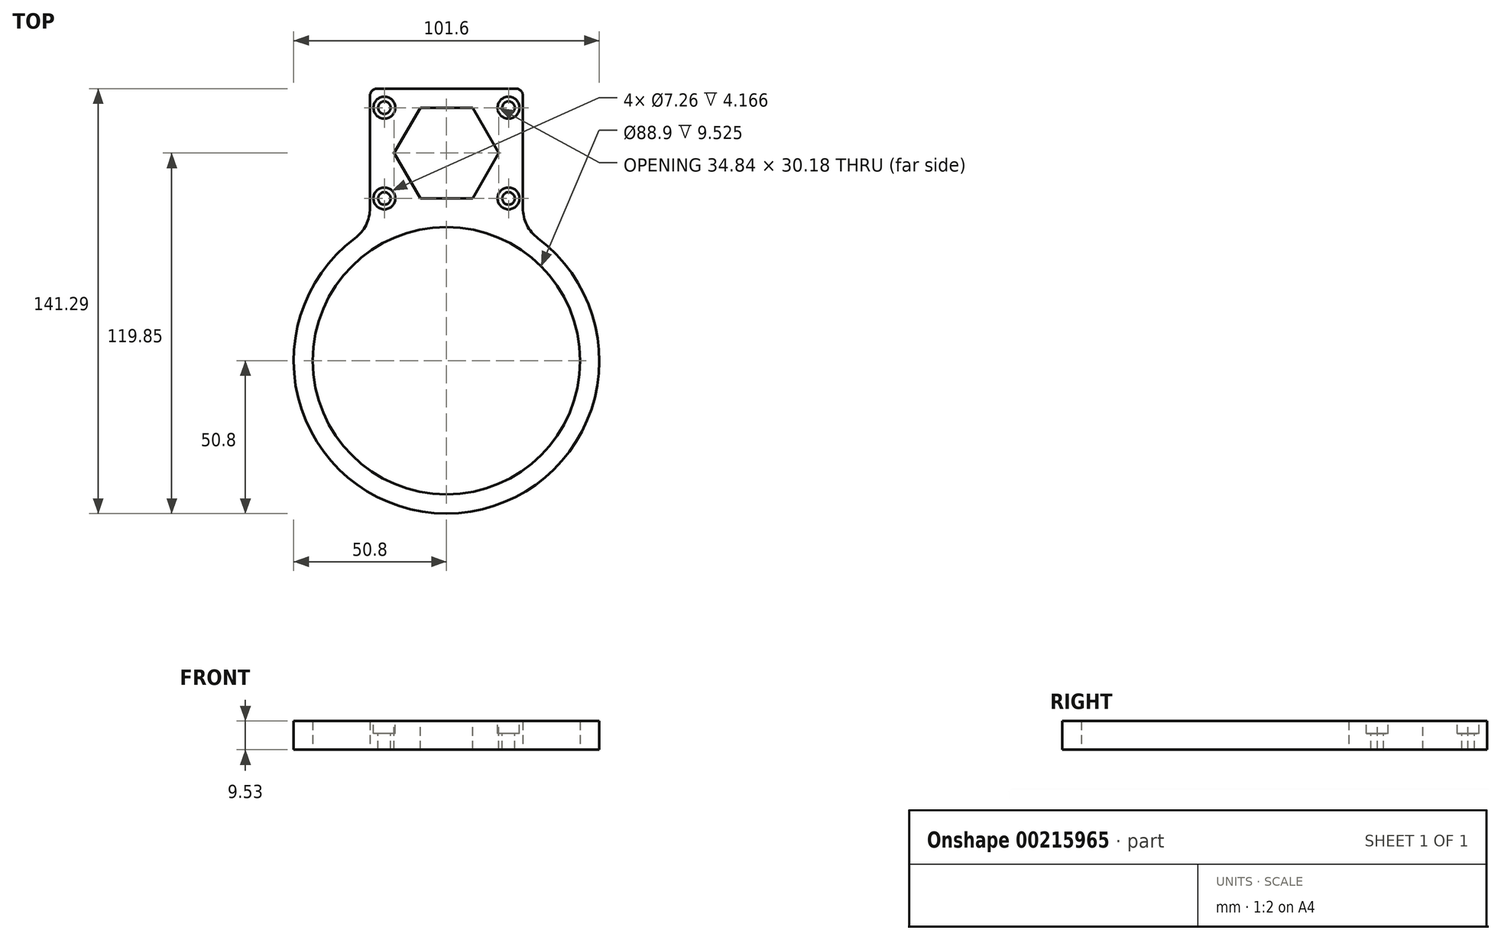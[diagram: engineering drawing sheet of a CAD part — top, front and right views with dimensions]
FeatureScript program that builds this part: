
annotation { "Feature Type Name" : "Feature", "Feature Type Description" : "" }
export const myFeature = defineFeature(function(context is Context, id is Id, definition is map)
    precondition{}
    {
        {
            var Q0;
            Q0=qCreatedBy(makeId("Top.planeOp"),FACE);
            var sketch = newSketch(context, id + "F0", { "sketchPlane" : qUnion([Q0])});
            skCircle(sketch, "E0", {"center": v(0, 0) * mm, "radius": 44.45 * mm});
            skArc(sketch, "E1", {"start": v(-25.4, 44) * mm, "mid": v(0, -50.8) * mm, "end": v(25.4, 44) * mm});
            skLineSegment(sketch, "E2", {"start": v(-25.4, 44) * mm, "end": v(-25.4, 90.49) * mm});
            skLineSegment(sketch, "E3", {"start": v(-25.4, 90.49) * mm, "end": v(25.4, 90.49) * mm});
            skLineSegment(sketch, "E4", {"start": v(25.4, 90.49) * mm, "end": v(25.4, 44) * mm});
            skLineSegment(sketch, "E5", {"start": v(0, 143.03) * mm, "end": v(0, 0) * mm, "construction": true});
            skSolve(sketch);
        }
        {
            var Q0;
            Q0=makeQuery(id+"F0.imprint","IMPRINT",FACE,{"disambiguationData":[TD([[makeQuery(id+"F0.imprint","IMPRINT",EDGE,{"derivedFrom":sQuery(id+"F0.wireOp",EDGE,"E0")}),-1.0]])]});
            extrude(context, id + "F1", {"entities" : qUnion([Q0]), "depth" : 9.52 * mm});
        }
        {
            var Q0;
            Q0=makeQuery(id+"F1.opExtrude","CAP_FACE",FACE,{"disambiguationData":[OSD([sQuery(id+"F0.wireOp",EDGE,"E0"),sQuery(id+"F0.wireOp",EDGE,"E1"),sQuery(id+"F0.wireOp",EDGE,"E2"),sQuery(id+"F0.wireOp",EDGE,"E3"),sQuery(id+"F0.wireOp",EDGE,"E4")])],"isStart":false});
            var sketch = newSketch(context, id + "F2", { "sketchPlane" : qUnion([Q0])});
            skLineSegment(sketch, "E6.bottom", {"start": v(-20.64, 84.14) * mm, "end": v(20.64, 84.14) * mm, "construction": true});
            skLineSegment(sketch, "E6.top", {"start": v(-20.64, 53.96) * mm, "end": v(20.64, 53.96) * mm, "construction": true});
            skLineSegment(sketch, "E6.left", {"start": v(-20.64, 84.14) * mm, "end": v(-20.64, 53.96) * mm, "construction": true});
            skLineSegment(sketch, "E6.right", {"start": v(20.64, 84.14) * mm, "end": v(20.64, 53.96) * mm, "construction": true});
            skCircle(sketch, "E7", {"center": v(-20.64, 84.14) * mm, "radius": 2.08 * mm});
            skCircle(sketch, "E8", {"center": v(20.64, 84.14) * mm, "radius": 2.08 * mm});
            skCircle(sketch, "E9", {"center": v(20.64, 53.96) * mm, "radius": 2.08 * mm});
            skCircle(sketch, "E10", {"center": v(-20.64, 53.96) * mm, "radius": 2.08 * mm});
            skCircle(sketch, "E11.cCircle", {"center": v(0, 69.05) * mm, "radius": 15.09 * mm, "construction": true});
            skLineSegment(sketch, "E11.0", {"start": v(-8.71, 53.96) * mm, "end": v(-17.42, 69.05) * mm});
            skLineSegment(sketch, "E11.1", {"start": v(-17.42, 69.05) * mm, "end": v(-8.71, 84.14) * mm});
            skLineSegment(sketch, "E11.2", {"start": v(-8.71, 84.14) * mm, "end": v(8.71, 84.14) * mm});
            skLineSegment(sketch, "E11.3", {"start": v(8.71, 84.14) * mm, "end": v(17.42, 69.05) * mm});
            skLineSegment(sketch, "E11.4", {"start": v(17.42, 69.05) * mm, "end": v(8.71, 53.96) * mm});
            skLineSegment(sketch, "E11.5", {"start": v(8.71, 53.96) * mm, "end": v(-8.71, 53.96) * mm});
            skPoint(sketch, "E11.0.midPoint", {"position": v(-13.07, 61.5) * mm});
            skSolve(sketch);
        }
        {
            var Q0;
            Q0=qSketchRegion(id+"F2",true);
            extrude(context, id + "F3", {"entities" : qUnion([Q0]), "operationType" : NewBodyOperationType.REMOVE, "oppositeDirection" : true, "depth" : 25.4 * mm});
        }
        {
            var Q0;
            Q0=makeQuery(id+"F1.opExtrude","CAP_FACE",FACE,{"disambiguationData":[OSD([sQuery(id+"F0.wireOp",EDGE,"E0"),sQuery(id+"F0.wireOp",EDGE,"E1"),sQuery(id+"F0.wireOp",EDGE,"E2"),sQuery(id+"F0.wireOp",EDGE,"E3"),sQuery(id+"F0.wireOp",EDGE,"E4")])],"isStart":false});
            var sketch = newSketch(context, id + "F4", { "sketchPlane" : qUnion([Q0])});
            skCircle(sketch, "E12", {"center": v(-20.64, 84.14) * mm, "radius": 3.63 * mm});
            skCircle(sketch, "E13", {"center": v(20.64, 84.14) * mm, "radius": 3.63 * mm});
            skCircle(sketch, "E14", {"center": v(20.64, 53.96) * mm, "radius": 3.63 * mm});
            skCircle(sketch, "E15", {"center": v(-20.64, 53.96) * mm, "radius": 3.63 * mm});
            skSolve(sketch);
        }
        {
            var Q0;
            Q0=qSketchRegion(id+"F4",true);
            extrude(context, id + "F5", {"entities" : qUnion([Q0]), "operationType" : NewBodyOperationType.REMOVE, "oppositeDirection" : true, "depth" : 4.17 * mm});
        }
        {
            var Q0;
            Q0=makeQuery(id+"F1.opExtrude","SWEPT_EDGE",EDGE,{"disambiguationData":[OSD([sQuery(id+"F0.wireOp",EDGE,"E2"),sQuery(id+"F0.wireOp",EDGE,"E3")])]});
            var Q1;
            Q1=makeQuery(id+"F1.opExtrude","SWEPT_EDGE",EDGE,{"disambiguationData":[OSD([sQuery(id+"F0.wireOp",EDGE,"E3"),sQuery(id+"F0.wireOp",EDGE,"E4")])]});
            fillet(context, id + "F6", {"entities" : qUnion([Q0, Q1]), "radius" : 2.38 * mm, "tangentPropagation" : true, "allowEdgeOverflow" : false});
        }
        {
            var Q0;
            Q0=makeQuery(id+"F1.opExtrude","SWEPT_EDGE",EDGE,{"disambiguationData":[OSD([sQuery(id+"F0.wireOp",EDGE,"E1"),sQuery(id+"F0.wireOp",EDGE,"E2")])]});
            var Q1;
            Q1=makeQuery(id+"F1.opExtrude","SWEPT_EDGE",EDGE,{"disambiguationData":[OSD([sQuery(id+"F0.wireOp",EDGE,"E1"),sQuery(id+"F0.wireOp",EDGE,"E4")])]});
            fillet(context, id + "F7", {"entities" : qUnion([Q0, Q1]), "radius" : 12.7 * mm, "tangentPropagation" : true, "allowEdgeOverflow" : false});
        }
    });
